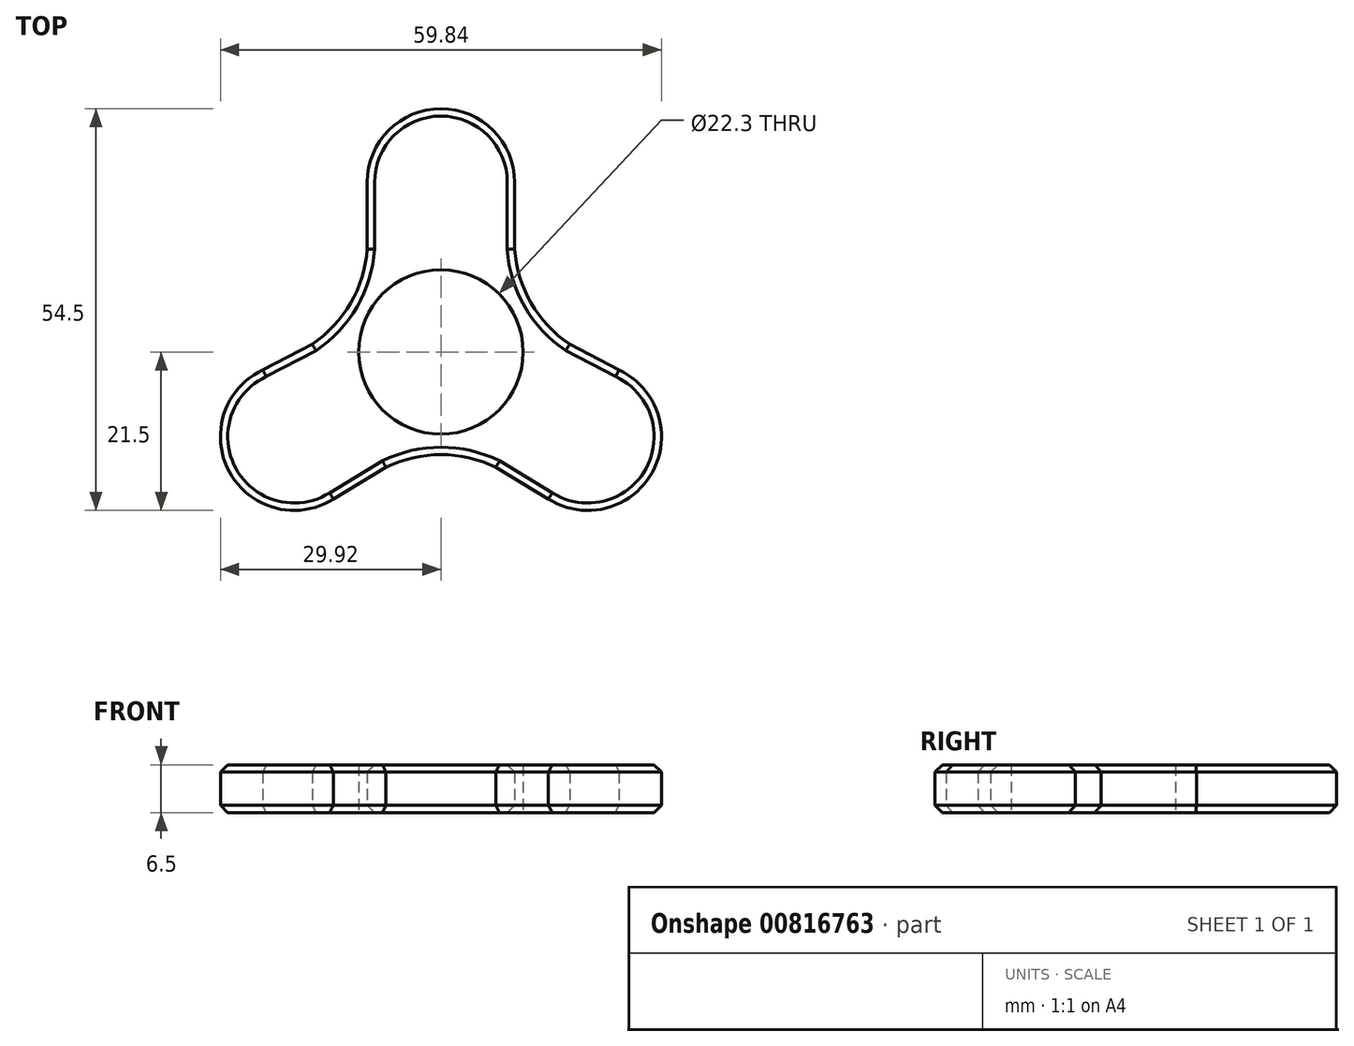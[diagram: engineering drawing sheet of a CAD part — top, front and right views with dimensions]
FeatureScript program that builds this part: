
annotation { "Feature Type Name" : "Feature", "Feature Type Description" : "" }
export const myFeature = defineFeature(function(context is Context, id is Id, definition is map)
    precondition{}
    {
        {
            var Q0;
            Q0=qCreatedBy(makeId("Top.planeOp"),FACE);
            var sketch = newSketch(context, id + "F0", { "sketchPlane" : qUnion([Q0])});
            skCircle(sketch, "E0", {"center": v(0, 0) * mm, "radius": 11.15 * mm});
            skLineSegment(sketch, "E1", {"start": v(0, 0) * mm, "end": v(0, 23) * mm});
            skCircle(sketch, "E2", {"center": v(0, 23) * mm, "radius": 10 * mm});
            skCircle(sketch, "E3.cCircle", {"center": v(0, 0) * mm, "radius": 23 * mm, "construction": true});
            skLineSegment(sketch, "E3.0", {"start": v(0, 23) * mm, "end": v(19.92, -11.5) * mm});
            skLineSegment(sketch, "E3.1", {"start": v(19.92, -11.5) * mm, "end": v(-19.92, -11.5) * mm});
            skLineSegment(sketch, "E3.2", {"start": v(-19.92, -11.5) * mm, "end": v(0, 23) * mm});
            skCircle(sketch, "E4", {"center": v(-19.92, -11.5) * mm, "radius": 10 * mm});
            skCircle(sketch, "E5", {"center": v(19.92, -11.5) * mm, "radius": 10 * mm});
            skLineSegment(sketch, "E6", {"start": v(0, 23) * mm, "end": v(-10, 23) * mm});
            skLineSegment(sketch, "E7", {"start": v(-10, 23) * mm, "end": v(-10, 4.93) * mm});
            skLineSegment(sketch, "E8", {"start": v(0, 23) * mm, "end": v(10, 23) * mm});
            skLineSegment(sketch, "E9", {"start": v(10, 23) * mm, "end": v(10, 4.93) * mm});
            skLineSegment(sketch, "E10", {"start": v(19.92, -11.5) * mm, "end": v(24.92, -2.84) * mm});
            skLineSegment(sketch, "E11", {"start": v(19.92, -11.5) * mm, "end": v(14.92, -20.16) * mm});
            skLineSegment(sketch, "E12", {"start": v(-19.92, -11.5) * mm, "end": v(-14.92, -20.16) * mm});
            skLineSegment(sketch, "E13", {"start": v(-19.92, -11.5) * mm, "end": v(-24.92, -2.84) * mm});
            skLineSegment(sketch, "E14", {"start": v(-24.92, -2.84) * mm, "end": v(-10, 4.93) * mm});
            skLineSegment(sketch, "E15", {"start": v(10, 4.93) * mm, "end": v(24.92, -2.84) * mm});
            skLineSegment(sketch, "E16", {"start": v(0, 0) * mm, "end": v(0, -11.15) * mm});
            skLineSegment(sketch, "E17", {"start": v(0, -11.15) * mm, "end": v(-14.92, -20.16) * mm});
            skLineSegment(sketch, "E18", {"start": v(0, -11.15) * mm, "end": v(14.92, -20.16) * mm});
            skArc(sketch, "E19", {"start": v(-17.46, 1.05) * mm, "mid": v(-12.24, 6.64) * mm, "end": v(-10, 13.97) * mm});
            skArc(sketch, "E20", {"start": v(10, 13.97) * mm, "mid": v(12.24, 6.64) * mm, "end": v(17.46, 1.05) * mm});
            skArc(sketch, "E21", {"start": v(7.46, -15.66) * mm, "mid": v(0, -13.93) * mm, "end": v(-7.46, -15.66) * mm});
            skSolve(sketch);
        }
        {
            var Q0;
            Q0 = qSketchRegion(id + "F0", true);
            var Q1;
            {var subQ5=sQuery(id+"F0.wireOp",EDGE,"E17");var subQ6=sQuery(id+"F0.wireOp",EDGE,"E3.1");var subQ7=makeQuery(id+"F0.imprint","INTERSECT",VERTEX,{"derivedFrom":[subQ6,subQ5]});Q1=makeQuery(id+"F0.imprint","IMPRINT",FACE,{"disambiguationData":[TD([[makeQuery(id+"F0.imprint","IMPRINT",EDGE,{"disambiguationData":[TD([[subQ7,-1.0]])],"derivedFrom":subQ6}),-1.0]])]});}
            var Q2;
            {var subQ1=sQuery(id+"F0.wireOp",EDGE,"E3.1");var subQ3=sQuery(id+"F0.wireOp",EDGE,"E4");var subQ4=makeQuery(id+"F0.imprint","INTERSECT",VERTEX,{"derivedFrom":[subQ1,subQ3]});Q2=makeQuery(id+"F0.imprint","IMPRINT",FACE,{"disambiguationData":[TD([[makeQuery(id+"F0.imprint","IMPRINT",EDGE,{"disambiguationData":[TD([[subQ4,-1.0]])],"derivedFrom":subQ3}),1.0]])]});}
            var Q3;
            {var subQ0=sQuery(id+"F0.wireOp",EDGE,"E14");var subQ1=sQuery(id+"F0.wireOp",EDGE,"E3.2");var subQ2=makeQuery(id+"F0.imprint","INTERSECT",VERTEX,{"derivedFrom":[subQ1,subQ0]});Q3=makeQuery(id+"F0.imprint","IMPRINT",FACE,{"disambiguationData":[TD([[makeQuery(id+"F0.imprint","IMPRINT",EDGE,{"disambiguationData":[TD([[subQ2,-1.0]])],"derivedFrom":subQ1}),-1.0]])]});}
            var Q4;
            {var subQ1=sQuery(id+"F0.wireOp",EDGE,"E1");var subQ6=sQuery(id+"F0.wireOp",EDGE,"E0");var subQ9=makeQuery(id+"F0.imprint","INTERSECT",VERTEX,{"derivedFrom":[subQ6,subQ1]});Q4=makeQuery(id+"F0.imprint","IMPRINT",FACE,{"disambiguationData":[TD([[makeQuery(id+"F0.imprint","IMPRINT",EDGE,{"disambiguationData":[TD([[subQ9,-1.0]])],"derivedFrom":subQ1}),1.0]])]});}
            var Q5;
            {var subQ1=sQuery(id+"F0.wireOp",EDGE,"E1");var subQ3=sQuery(id+"F0.wireOp",EDGE,"E2");var subQ4=makeQuery(id+"F0.imprint","INTERSECT",VERTEX,{"derivedFrom":[subQ1,subQ3]});Q5=makeQuery(id+"F0.imprint","IMPRINT",FACE,{"disambiguationData":[TD([[makeQuery(id+"F0.imprint","IMPRINT",EDGE,{"disambiguationData":[TD([[subQ4,1.0]])],"derivedFrom":subQ3}),1.0]])]});}
            var Q6;
            {var subQ1=sQuery(id+"F0.wireOp",EDGE,"E1");var subQ3=sQuery(id+"F0.wireOp",EDGE,"E2");var subQ4=makeQuery(id+"F0.imprint","INTERSECT",VERTEX,{"derivedFrom":[subQ1,subQ3]});Q6=makeQuery(id+"F0.imprint","IMPRINT",FACE,{"disambiguationData":[TD([[makeQuery(id+"F0.imprint","IMPRINT",EDGE,{"disambiguationData":[TD([[subQ4,-1.0]])],"derivedFrom":subQ3}),1.0]])]});}
            var Q7;
            {var subQ5=sQuery(id+"F0.wireOp",EDGE,"E0");var subQ7=sQuery(id+"F0.wireOp",EDGE,"E1");var subQ9=makeQuery(id+"F0.imprint","INTERSECT",VERTEX,{"derivedFrom":[subQ5,subQ7]});Q7=makeQuery(id+"F0.imprint","IMPRINT",FACE,{"disambiguationData":[TD([[makeQuery(id+"F0.imprint","IMPRINT",EDGE,{"disambiguationData":[TD([[subQ9,-1.0]])],"derivedFrom":subQ7}),-1.0]])]});}
            var Q8;
            {var subQ0=sQuery(id+"F0.wireOp",EDGE,"E9");var subQ1=sQuery(id+"F0.wireOp",EDGE,"E3.0");var subQ2=makeQuery(id+"F0.imprint","INTERSECT",VERTEX,{"derivedFrom":[subQ1,subQ0]});Q8=makeQuery(id+"F0.imprint","IMPRINT",FACE,{"disambiguationData":[TD([[makeQuery(id+"F0.imprint","IMPRINT",EDGE,{"disambiguationData":[TD([[subQ2,-1.0]])],"derivedFrom":subQ1}),-1.0]])]});}
            var Q9;
            {var subQ1=sQuery(id+"F0.wireOp",EDGE,"E3.0");var subQ5=sQuery(id+"F0.wireOp",EDGE,"E15");var subQ6=makeQuery(id+"F0.imprint","INTERSECT",VERTEX,{"derivedFrom":[subQ1,subQ5]});Q9=makeQuery(id+"F0.imprint","IMPRINT",FACE,{"disambiguationData":[TD([[makeQuery(id+"F0.imprint","IMPRINT",EDGE,{"disambiguationData":[TD([[subQ6,-1.0]])],"derivedFrom":subQ1}),-1.0]])]});}
            var Q10;
            {var subQ1=sQuery(id+"F0.wireOp",EDGE,"E3.0");var subQ3=sQuery(id+"F0.wireOp",EDGE,"E5");var subQ4=makeQuery(id+"F0.imprint","INTERSECT",VERTEX,{"derivedFrom":[subQ1,subQ3]});Q10=makeQuery(id+"F0.imprint","IMPRINT",FACE,{"disambiguationData":[TD([[makeQuery(id+"F0.imprint","IMPRINT",EDGE,{"disambiguationData":[TD([[subQ4,-1.0]])],"derivedFrom":subQ3}),1.0]])]});}
            var Q11;
            {var subQ0=sQuery(id+"F0.wireOp",EDGE,"E18");var subQ1=sQuery(id+"F0.wireOp",EDGE,"E3.1");var subQ2=makeQuery(id+"F0.imprint","INTERSECT",VERTEX,{"derivedFrom":[subQ1,subQ0]});Q11=makeQuery(id+"F0.imprint","IMPRINT",FACE,{"disambiguationData":[TD([[makeQuery(id+"F0.imprint","IMPRINT",EDGE,{"disambiguationData":[TD([[subQ2,-1.0]])],"derivedFrom":subQ1}),-1.0]])]});}
            var Q12;
            {var subQ0=sQuery(id+"F0.wireOp",EDGE,"E3.2");var subQ1=sQuery(id+"F0.wireOp",EDGE,"E0");var subQ2=makeQuery(id+"F0.imprint","INTERSECT",VERTEX,{"disambiguationData":[OD(1.0)],"derivedFrom":[subQ1,subQ0]});Q12=makeQuery(id+"F0.imprint","IMPRINT",FACE,{"disambiguationData":[TD([[makeQuery(id+"F0.imprint","IMPRINT",EDGE,{"disambiguationData":[TD([[subQ2,-1.0]])],"derivedFrom":subQ1}),-1.0]])]});}
            var Q13;
            {var subQ0=sQuery(id+"F0.wireOp",EDGE,"E3.0");var subQ1=sQuery(id+"F0.wireOp",EDGE,"E0");var subQ2=makeQuery(id+"F0.imprint","INTERSECT",VERTEX,{"disambiguationData":[OD(0.0)],"derivedFrom":[subQ1,subQ0]});Q13=makeQuery(id+"F0.imprint","IMPRINT",FACE,{"disambiguationData":[TD([[makeQuery(id+"F0.imprint","IMPRINT",EDGE,{"disambiguationData":[TD([[subQ2,1.0]])],"derivedFrom":subQ1}),-1.0]])]});}
            extrude(context, id + "F1", {"entities" : qUnion([Q0, Q1, Q2, Q3, Q4, Q5, Q6, Q7, Q8, Q9, Q10, Q11, Q12, Q13]), "depth" : 6.5 * mm, "offsetDistance" : 25 * mm});
        }
        {
            var Q0;
            Q0=makeQuery(id+"F1.opExtrude","CAP_EDGE",EDGE,{"disambiguationData":[OSD([sQuery(id+"F0.wireOp",EDGE,"E4")])],"isStart":false});
            var Q1;
            Q1=makeQuery(id+"F1.opExtrude","CAP_EDGE",EDGE,{"disambiguationData":[OSD([sQuery(id+"F0.wireOp",EDGE,"E5")])],"isStart":false});
            var Q2;
            Q2=makeQuery(id+"F1.opExtrude","CAP_EDGE",EDGE,{"disambiguationData":[OSD([sQuery(id+"F0.wireOp",EDGE,"E2")])],"isStart":false});
            var Q3;
            Q3=makeQuery(id+"F1.opExtrude","CAP_EDGE",EDGE,{"disambiguationData":[OSD([sQuery(id+"F0.wireOp",EDGE,"E5")])],"isStart":true});
            var Q4;
            Q4=makeQuery(id+"F1.opExtrude","CAP_EDGE",EDGE,{"disambiguationData":[OSD([sQuery(id+"F0.wireOp",EDGE,"E4")])],"isStart":true});
            var Q5;
            Q5=makeQuery(id+"F1.opExtrude","CAP_EDGE",EDGE,{"disambiguationData":[OSD([sQuery(id+"F0.wireOp",EDGE,"E9")])],"isStart":false});
            var Q6;
            Q6=makeQuery(id+"F1.opExtrude","CAP_EDGE",EDGE,{"disambiguationData":[OSD([sQuery(id+"F0.wireOp",EDGE,"E20")])],"isStart":false});
            var Q7;
            Q7=makeQuery(id+"F1.opExtrude","CAP_EDGE",EDGE,{"disambiguationData":[OSD([sQuery(id+"F0.wireOp",EDGE,"E15")])],"isStart":false});
            var Q8;
            Q8=makeQuery(id+"F1.opExtrude","CAP_EDGE",EDGE,{"disambiguationData":[OSD([sQuery(id+"F0.wireOp",EDGE,"E21")])],"isStart":false});
            var Q9;
            Q9=makeQuery(id+"F1.opExtrude","CAP_EDGE",EDGE,{"disambiguationData":[OSD([sQuery(id+"F0.wireOp",EDGE,"E17")])],"isStart":false});
            var Q10;
            Q10=makeQuery(id+"F1.opExtrude","CAP_EDGE",EDGE,{"disambiguationData":[OSD([sQuery(id+"F0.wireOp",EDGE,"E14")])],"isStart":false});
            var Q11;
            Q11=makeQuery(id+"F1.opExtrude","CAP_EDGE",EDGE,{"disambiguationData":[OSD([sQuery(id+"F0.wireOp",EDGE,"E19")])],"isStart":false});
            var Q12;
            Q12=makeQuery(id+"F1.opExtrude","CAP_EDGE",EDGE,{"disambiguationData":[OSD([sQuery(id+"F0.wireOp",EDGE,"E7")])],"isStart":false});
            var Q13;
            Q13=makeQuery(id+"F1.opExtrude","CAP_EDGE",EDGE,{"disambiguationData":[OSD([sQuery(id+"F0.wireOp",EDGE,"E18")])],"isStart":false});
            var Q14;
            Q14=makeQuery(id+"F1.opExtrude","CAP_EDGE",EDGE,{"disambiguationData":[OSD([sQuery(id+"F0.wireOp",EDGE,"E18")])],"isStart":true});
            var Q15;
            Q15=makeQuery(id+"F1.opExtrude","CAP_EDGE",EDGE,{"disambiguationData":[OSD([sQuery(id+"F0.wireOp",EDGE,"E21")])],"isStart":true});
            var Q16;
            Q16=makeQuery(id+"F1.opExtrude","CAP_EDGE",EDGE,{"disambiguationData":[OSD([sQuery(id+"F0.wireOp",EDGE,"E17")])],"isStart":true});
            var Q17;
            Q17=makeQuery(id+"F1.opExtrude","CAP_EDGE",EDGE,{"disambiguationData":[OSD([sQuery(id+"F0.wireOp",EDGE,"E14")])],"isStart":true});
            var Q18;
            Q18=makeQuery(id+"F1.opExtrude","CAP_EDGE",EDGE,{"disambiguationData":[OSD([sQuery(id+"F0.wireOp",EDGE,"E19")])],"isStart":true});
            var Q19;
            Q19=makeQuery(id+"F1.opExtrude","CAP_EDGE",EDGE,{"disambiguationData":[OSD([sQuery(id+"F0.wireOp",EDGE,"E7")])],"isStart":true});
            var Q20;
            Q20=makeQuery(id+"F1.opExtrude","CAP_EDGE",EDGE,{"disambiguationData":[OSD([sQuery(id+"F0.wireOp",EDGE,"E2")])],"isStart":true});
            var Q21;
            Q21=makeQuery(id+"F1.opExtrude","CAP_EDGE",EDGE,{"disambiguationData":[OSD([sQuery(id+"F0.wireOp",EDGE,"E15")])],"isStart":true});
            var Q22;
            Q22=makeQuery(id+"F1.opExtrude","CAP_EDGE",EDGE,{"disambiguationData":[OSD([sQuery(id+"F0.wireOp",EDGE,"E20")])],"isStart":true});
            chamfer(context, id + "F2", {"entities" : qUnion([Q0, Q1, Q2, Q3, Q4, Q5, Q6, Q7, Q8, Q9, Q10, Q11, Q12, Q13, Q14, Q15, Q16, Q17, Q18, Q19, Q20, Q21, Q22]), "width" : 1 * mm, "tangentPropagation" : true});
        }
    });
